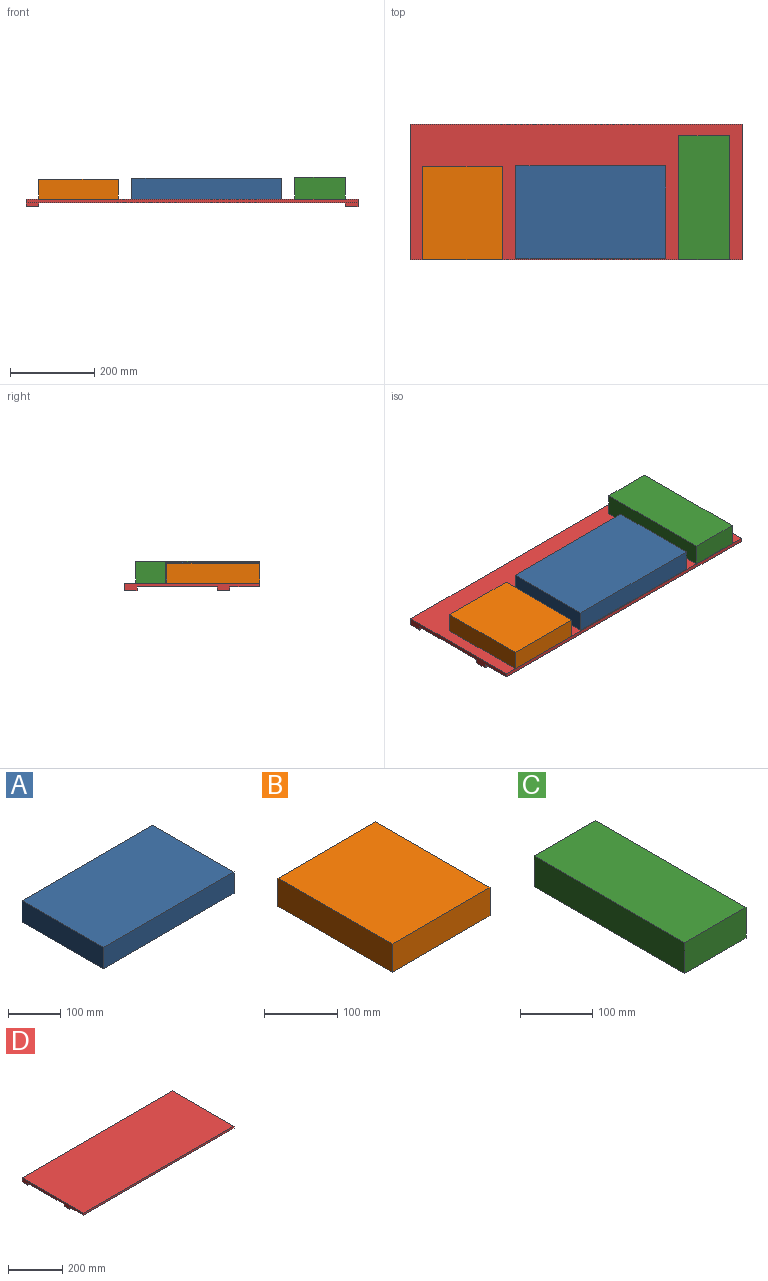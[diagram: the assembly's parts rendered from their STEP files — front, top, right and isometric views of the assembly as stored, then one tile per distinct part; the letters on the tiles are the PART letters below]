
ASSEMBLY  parts=4 mates=3
PART A: 6 faces, bbox 355x220x50 mm
  f0: plane 355x50mm, normal (0,1,0), area 17750mm2, adj f1,f3,f4,f5
  f1: plane 220x50mm, normal (-1,0,0), area 11000mm2, adj f0,f2,f4,f5
  f2: plane 355x50mm, normal (0,-1,0), area 17750mm2, adj f1,f3,f4,f5
  f3: plane 220x50mm, normal (1,0,0), area 11000mm2, adj f0,f2,f4,f5
  f4: plane 355x220mm, normal (0,0,1), area 78100mm2, adj f0,f1,f2,f3
  f5: plane 355x220mm, normal (0,0,-1), area 78100mm2, adj f0,f1,f2,f3
PART B: 6 faces, bbox 189x220x47 mm
  f0: plane 189x47mm, normal (0,1,0), area 8883mm2, adj f1,f3,f4,f5
  f1: plane 220x47mm, normal (-1,0,0), area 10340mm2, adj f0,f2,f4,f5
  f2: plane 189x47mm, normal (0,-1,0), area 8883mm2, adj f1,f3,f4,f5
  f3: plane 220x47mm, normal (1,0,0), area 10340mm2, adj f0,f2,f4,f5
  f4: plane 220x189mm, normal (0,0,1), area 41580mm2, adj f0,f1,f2,f3
  f5: plane 220x189mm, normal (0,0,-1), area 41580mm2, adj f0,f1,f2,f3
PART C: 6 faces, bbox 120x294x52 mm
  f0: plane 120x52mm, normal (0,1,0), area 6240mm2, adj f1,f3,f4,f5
  f1: plane 294x52mm, normal (-1,0,0), area 15288mm2, adj f0,f2,f4,f5
  f2: plane 120x52mm, normal (0,-1,0), area 6240mm2, adj f1,f3,f4,f5
  f3: plane 294x52mm, normal (1,0,0), area 15288mm2, adj f0,f2,f4,f5
  f4: plane 294x120mm, normal (0,0,1), area 35280mm2, adj f0,f1,f2,f3
  f5: plane 294x120mm, normal (0,0,-1), area 35280mm2, adj f0,f1,f2,f3
PART D: 20 faces, bbox 787.8x320.4x18 mm
  f0: plane 787.76x320.44mm, normal (0,0,-1), area 248842.7mm2, adj f1,f2,f3,f4,f7,f8,f9,f10
  f1: plane 787.76x18mm, normal (0,1,0), area 7629.8mm2, adj f0,f2,f4,f5,f6,f8,f13,f15
  f2: plane 320.44x18mm, normal (-1,0,0), area 3422.3mm2, adj f0,f1,f3,f5,f6,f7,f9,f10
  f3: plane 787.76x9mm, normal (0,-1,0), area 7089.8mm2, adj f0,f2,f4,f5
  f4: plane 320.44x18mm, normal (1,0,0), area 3422.3mm2, adj f0,f1,f3,f5,f13,f14,f16,f17
  f5: plane 787.76x320.44mm, normal (0,0,1), area 252431.7mm2, adj f1,f2,f3,f4
  f6: plane 30x29.82mm, normal (0,0,-1), area 894.5mm2, adj f1,f2,f7,f8
  f7: plane 30x9mm, normal (0,-1,0), area 270mm2, adj f0,f2,f6,f8
  f8: plane 29.82x9mm, normal (1,0,0), area 268.4mm2, adj f0,f1,f6,f7
  f9: plane 30x9mm, normal (0,-1,0), area 270mm2, adj f0,f2,f11,f12
  f10: plane 30x9mm, normal (0,1,0), area 270mm2, adj f0,f2,f11,f12
  f11: plane 30x30mm, normal (0,0,-1), area 900mm2, adj f2,f9,f10,f12
  f12: plane 30x9mm, normal (1,0,0), area 270mm2, adj f0,f9,f10,f11
  f13: plane 30x29.82mm, normal (0,0,-1), area 894.5mm2, adj f1,f4,f14,f15
  f14: plane 30x9mm, normal (0,-1,0), area 270mm2, adj f0,f4,f13,f15
  f15: plane 29.82x9mm, normal (-1,0,0), area 268.4mm2, adj f0,f1,f13,f14
  f16: plane 30x9mm, normal (0,-1,0), area 270mm2, adj f0,f4,f18,f19
  f17: plane 30x9mm, normal (0,1,0), area 270mm2, adj f0,f4,f18,f19
  f18: plane 30x30mm, normal (0,0,-1), area 900mm2, adj f4,f16,f17,f19
  f19: plane 30x9mm, normal (-1,0,0), area 270mm2, adj f0,f16,f17,f18
PLACE A t=(-45.52,14.46,77.12)mm
PLACE B t=(-349.9,12.24,77.12)mm
PLACE C t=(223.36,49.24,77.12)mm
PLACE D t=(-80.52,62.46,68.12)mm
MATE fastened D.f5 <-> A.f5  axis (0,0,1) through (-80.52,62.46,77.12)mm
MATE fastened B.f5 <-> D.f5  axis (0,0,-1) through (-444.4,-97.76,77.12)mm
MATE fastened C.f5 <-> D.f5  axis (0,0,-1) through (283.36,-97.76,77.12)mm
